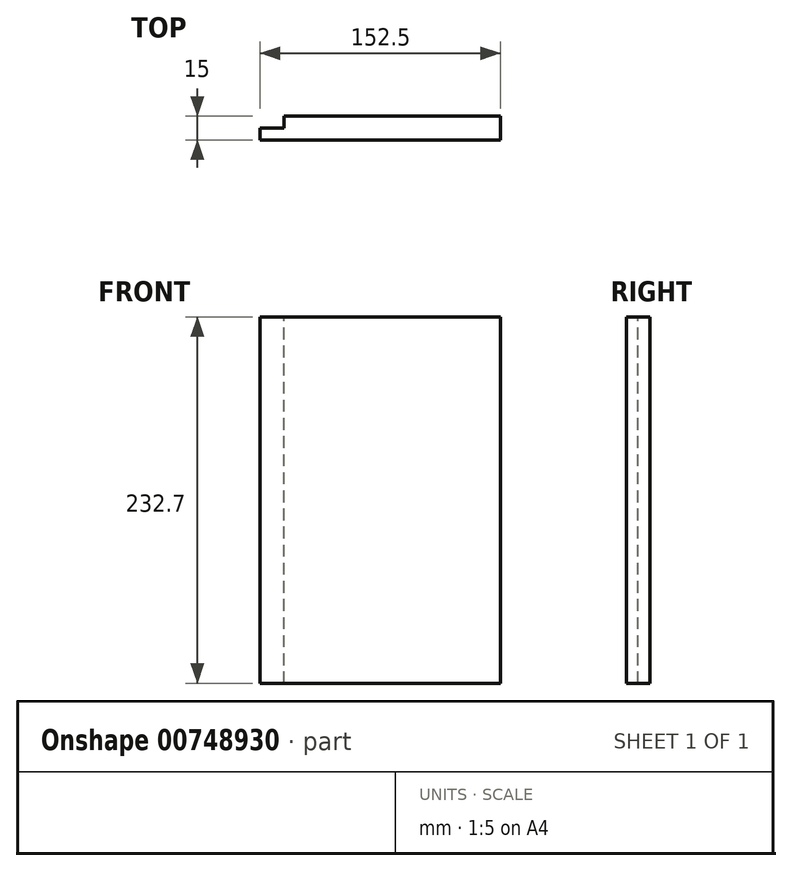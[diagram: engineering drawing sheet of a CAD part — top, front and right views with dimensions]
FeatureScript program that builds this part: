
annotation { "Feature Type Name" : "Feature", "Feature Type Description" : "" }
export const myFeature = defineFeature(function(context is Context, id is Id, definition is map)
    precondition{}
    {
        {
            var Q0;
            Q0=qCreatedBy(makeId("Top.planeOp"),FACE);
            var sketch = newSketch(context, id + "F0", { "sketchPlane" : qUnion([Q0])});
            skLineSegment(sketch, "E0.top", {"start": v(-33.67, -4.26) * mm, "end": v(-178.67, -4.26) * mm});
            skLineSegment(sketch, "E0.right", {"start": v(-178.67, 3.24) * mm, "end": v(-178.67, -4.26) * mm});
            skLineSegment(sketch, "E1", {"start": v(-163.67, 10.74) * mm, "end": v(-33.67, 10.74) * mm});
            skLineSegment(sketch, "E2.bottom", {"start": v(-33.67, -4.26) * mm, "end": v(-26.17, -4.26) * mm});
            skLineSegment(sketch, "E2.top", {"start": v(-33.67, 10.74) * mm, "end": v(-26.17, 10.74) * mm});
            skLineSegment(sketch, "E3", {"start": v(-26.17, 10.74) * mm, "end": v(-26.17, -4.26) * mm});
            skPoint(sketch, "E2.right.end.orphan", {"position": v(-18.67, 10.74) * mm});
            skPoint(sketch, "E4.orphan", {"position": v(-18.67, -4.26) * mm});
            skLineSegment(sketch, "E5.top", {"start": v(-178.67, 3.24) * mm, "end": v(-163.67, 3.24) * mm});
            skLineSegment(sketch, "E5.right", {"start": v(-163.67, 10.74) * mm, "end": v(-163.67, 3.24) * mm});
            skSolve(sketch);
        }
        {
            var Q0;
            Q0=makeQuery(id+"F0.imprint","IMPRINT",FACE,{"disambiguationData":[TD([[makeQuery(id+"F0.imprint","IMPRINT",EDGE,{"derivedFrom":sQuery(id+"F0.wireOp",EDGE,"E0.top")}),-1.0]])]});
            extrude(context, id + "F1", {"entities" : qUnion([Q0]), "oppositeDirection" : true, "depth" : 232.7 * mm, "offsetDistance" : 25 * mm, "symmetric" : true});
        }
    });
